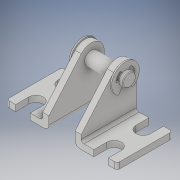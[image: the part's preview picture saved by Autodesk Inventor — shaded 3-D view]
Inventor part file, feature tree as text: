
AUTODESK INVENTOR PART (.ipt)
format: ipt  version: 2017 (Build 210142000, 142)  size: 245,760 bytes
history: native  units: in
note: dims shown in document units (in); Inventor stores cm internally (conversion verified against a paired STEP export)
features: fillet x2, revolve x1, other x1, mirror x1
ambient origin geometry x8: Origin, YZ Plane, XZ Plane, XY Plane, X Axis, Y Axis, Z Axis, Center Point
bodies: Solid1 (feature_tree), Solid2 (feature_tree), Solid3 (feature_tree), Solid4 (feature_tree), Solid5 (feature_tree)
feature tree (5):
  fillet  "Fillet2"  [1 undecoded]
  fillet  "Fillet4"  [1 undecoded]
  revolve  "Revolve1"  [1 undecoded]
  other  "Boss-Extrude5"
  mirror  "Mirror1"
note: 3 required parameter values undecoded (feature->parameter linkage not recoverable at this tier; creation-order binding heuristic only, values carry confidence <= 0.55)
